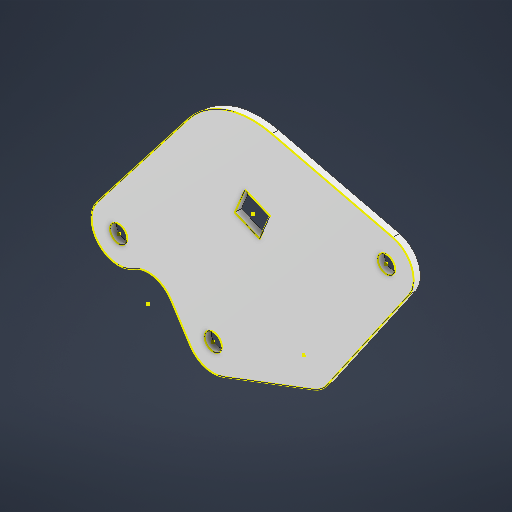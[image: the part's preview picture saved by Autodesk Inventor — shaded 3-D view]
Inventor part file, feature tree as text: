
AUTODESK INVENTOR PART (.ipt)
format: ipt  version: 2025 (Build 290162010, 162A)  size: 263,680 bytes
history: native  units: in
note: dims shown in document units (in); Inventor stores cm internally (conversion verified against a paired STEP export)
features: reference x7, other x6, sketch x2, sheet_metal_op x1
ambient origin geometry x8: Origin, YZ Plane, XZ Plane, XY Plane, X Axis, Y Axis, Z Axis, Center Point
bodies: Solid1 (feature_tree)
feature tree (16):
  sheet_metal_op  "Face1"
  sketch  "Sketch2"  dims[d3=0.16in d5=1.25in d6=0.16in d7=0.0687in d8=0.16in d10=0.16in d11=0.5in d12=0.5in d13=0.5in d14=0.16in d16=1.5in d17=0.5in d18=0.3624in d19=0.5in d20=0.0625in]
  sketch  "Sketch1"  dims[d0=2.5in]
  reference  "Reference1"
  reference  "Reference2"
  reference  "Reference3"
  reference  "Reference4"
  reference  "Reference5"
  reference  "Reference6"
  reference  "Reference7"
  other  "Plate1"
  parser-record x1  (decoder bookkeeping rows leaked as tree rows — omitted from the tree; the rows remain in map.json)
  other  "ACE 2.0.iam"
  other  "Shaft Collar without Set Screw:27"
  other  "V5 Rotation Sensor:1"
  other  "Insert Circle:16"
note: 1 file-system path scrubbed to <path> (originals preserved in map.json)
